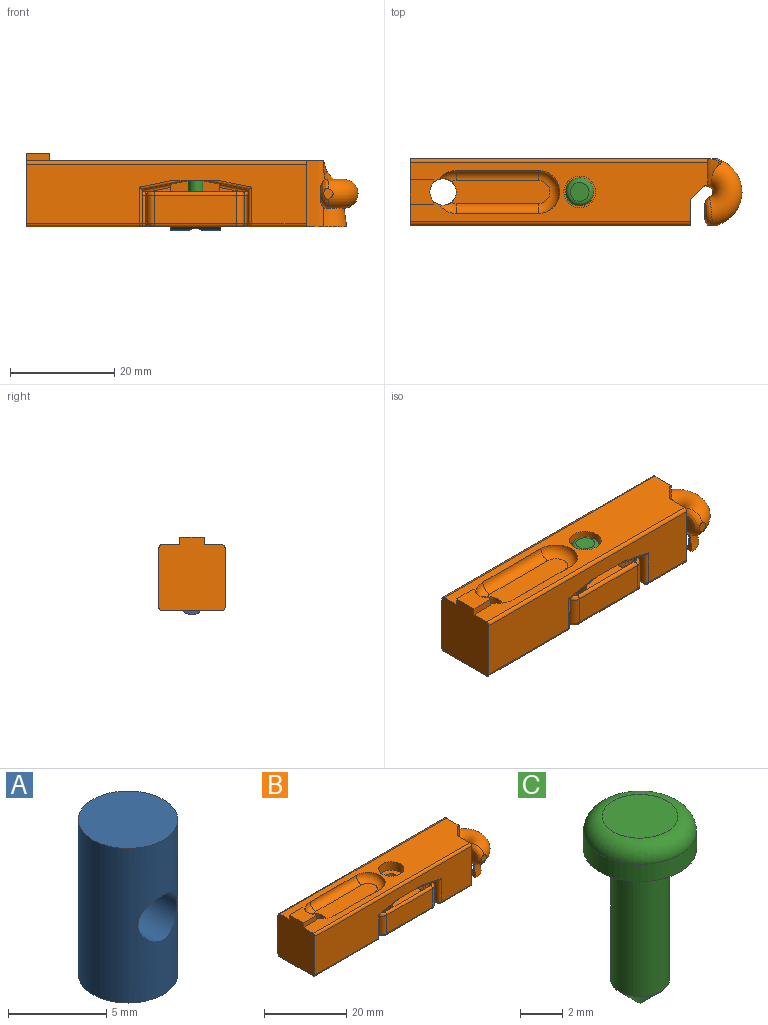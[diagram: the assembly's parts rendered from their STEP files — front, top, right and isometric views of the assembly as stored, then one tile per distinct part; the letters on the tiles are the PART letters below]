
ASSEMBLY  parts=3 mates=3
PART A: 4 faces, bbox 5.1x5.1x9.7 mm
  f0: cylinder r=2.54mm len=9.65mm, axis (0,0,-1), area 141.2mm2, adj f1,f2,f3
  f1: plane 5.08x5.08mm, normal (0,0,1), area 20.3mm2, adj f0
  f2: plane 5.08x5.08mm, normal (0,0,-1), area 20.3mm2, adj f0
  f3: cylinder r=1.4mm len=5.08mm, axis (0,-1,0), area 41mm2, adj f0
PART B: 172 faces, bbox 90.7x40.7x41.1 mm
  f0: plane 8.64x3.18mm, normal (0,0,-1), area 25.9mm2, adj f3,f124,f129,f130,f133,f134
  f1: torus R=3.81mm, axis (0,0,-1), area 204mm2, adj f6,f7,f10,f14,f29,f30,f33,f34
  f2: plane 57.24x11.49mm, normal (0,0,-1), area 414.8mm2, adj f8,f10,f15,f19,f26,f27,f45,f72
  f3: plane 9.4x1.14mm, normal (0,1,0), area 10.6mm2, adj f0,f60,f61,f68,f124,f129
  f4: plane 8.49x6.71mm, normal (-1,0,0), area 41.2mm2, adj f40,f45,f67,f140,f147,f148,f149,f153
  f5: cylinder r=1.59mm len=3.18mm, axis (0,0,1), area 12.8mm2, adj f38,f40,f41,f42,f43
  f6: cylinder r=6.35mm len=4.55mm, axis (0,0,-1), area 6.7mm2, adj f1,f14,f30,f35,f107,f157
  f7: plane 0.36x0.18mm, normal (0.91,-0.42,0), area 0mm2, adj f1,f29,f36
  f8: plane 2.9x1.42mm, normal (1,0,0), area 1.8mm2, adj f2,f10,f107
  f9: plane 57.24x11.49mm, normal (0,0,1), area 398mm2, adj f10,f11,f12,f15,f17,f18,f19,f21
  f10: cylinder r=1.27mm len=12.7mm, axis (0,0,-1), area 13.5mm2, adj f1,f2,f8,f9,f26,f28,f37,f107
  f11: plane 1.4x0.55mm, normal (1,0,0), area 0.8mm2, adj f9,f16,f18,f19
  f12: plane 1.4x0.55mm, normal (1,0,0), area 0.8mm2, adj f9,f16,f17,f19
  f13: plane 53.83x11.43mm, normal (0,-1,0), area 445mm2, adj f15,f27,f41,f109,f110,f111,f137,f140
  f14: plane 85.34x37.81mm, normal (0,1,0), area 656.6mm2, adj f1,f6,f15,f29,f154,f156
  f15: plane 14.1x12.7mm, normal (-1,0,0), area 167.5mm2, adj f2,f9,f13,f14,f16,f17,f18,f110
  f16: plane 4.72x4.57mm, normal (0,0,1), area 19.7mm2, adj f11,f12,f15,f17,f18,f19
  f17: plane 4.57x1.4mm, normal (0,-1,0), area 6.4mm2, adj f9,f12,f15,f16
  f18: plane 4.57x1.4mm, normal (0,1,0), area 6.4mm2, adj f9,f11,f15,f16
  f19: cylinder r=2.54mm len=14.1mm, axis (0,0,-1), area 194.8mm2, adj f2,f9,f11,f12,f16,f20,f21,f25
  f20: plane 18.94x4.45mm, normal (0,0,1), area 79.2mm2, adj f19,f21,f22,f23,f24,f25
  f21: torus R=2.22mm, axis (0,0,1), area 7.4mm2, adj f9,f19,f20,f22
  f22: cylinder r=1.91mm len=15.75mm, axis (1,0,0), area 47.1mm2, adj f9,f20,f21,f23
  f23: torus R=2.22mm, axis (0,0,1), area 32.3mm2, adj f9,f20,f22,f24
  f24: cylinder r=1.91mm len=15.75mm, axis (-1,0,0), area 47.1mm2, adj f9,f20,f23,f25
  f25: torus R=2.22mm, axis (0,0,1), area 7.4mm2, adj f9,f19,f20,f24
  f26: plane 12.7x2.42mm, normal (0.71,-0.71,0), area 43.5mm2, adj f2,f9,f10,f27
  f27: plane 12.7x4.83mm, normal (1,0,0), area 61.1mm2, adj f2,f9,f13,f26,f141,f160
  f28: plane 2.9x1.42mm, normal (1,0,0), area 1.8mm2, adj f9,f10,f108
  f29: cylinder r=6.35mm len=4.55mm, axis (0,0,-1), area 6.7mm2, adj f1,f7,f14,f36,f108,f155
  f30: plane 0.36x0.18mm, normal (0.91,-0.42,0), area 0mm2, adj f1,f6,f35
  f31: plane 3.12x3.05mm, normal (-1,0,0), area 7.5mm2, adj f34
  f32: plane 1.65x0.71mm, normal (-0.71,0.71,0), area 1.3mm2, adj f34
  f33: plane 28.49x28.17mm, normal (0,-1,0), area 2.8mm2, adj f1,f34
  f34: bspline ~5.59x5.58mm, area 25.5mm2, adj f1,f31,f32,f33,f101
  f35: cylinder r=1.27mm len=1.27mm, axis (0.42,0.91,0), area 0.8mm2, adj f1,f6,f30,f107
  f36: cylinder r=1.27mm len=1.27mm, axis (-0.42,-0.91,0), area 0.8mm2, adj f1,f7,f29,f108
  f37: bspline ~2.74x1.21mm, area 0mm2, adj f1,f10
  f38: plane 6.1x6.1mm, normal (0,0,1), area 21.3mm2, adj f5,f39
  f39: cylinder r=3.05mm len=6.1mm, axis (0,0,1), area 48.6mm2, adj f9,f38
  f40: plane 8.93x7.66mm, normal (-0.2,0,-0.98), area 68.5mm2, adj f4,f5,f41,f42,f137,f158
  f41: plane 9.02x5.49mm, normal (0,0,-1), area 13.5mm2, adj f5,f13,f40,f43,f109,f137
  f42: plane 2.54x1.04mm, normal (0,0,-1), area 1.3mm2, adj f5,f40,f43,f69
  f43: plane 8.99x7.72mm, normal (0.2,0,-0.98), area 68.8mm2, adj f5,f41,f42,f44,f109,f159
  f44: plane 8.49x6.71mm, normal (1,0,0), area 41.2mm2, adj f43,f45,f67,f111,f112,f113,f116,f117
  f45: plane 21.59x7.56mm, normal (0,-1,0), area 93.5mm2, adj f2,f4,f44,f69,f70,f71,f113,f153
  f46: plane 5.46x2.54mm, normal (0,-1,0), area 13.9mm2, adj f47,f117,f121,f162
  f47: cylinder r=0.76mm len=5.46mm, axis (0,0,-1), area 13.1mm2, adj f46,f48,f123,f163
  f48: plane 5.46x0.89mm, normal (0,1,0), area 4.9mm2, adj f47,f49,f127,f164
  f49: cylinder r=1.52mm len=5.46mm, axis (0,0,-1), area 26.1mm2, adj f48,f50,f132,f165
  f50: plane 15.75x5.46mm, normal (0,-1,0), area 86mm2, adj f49,f51,f134,f166
  f51: cylinder r=1.52mm len=5.46mm, axis (0,0,-1), area 26.1mm2, adj f50,f52,f136,f167
  f52: plane 5.46x0.89mm, normal (0,1,0), area 4.9mm2, adj f51,f53,f139,f168
  f53: cylinder r=0.76mm len=5.46mm, axis (0,0,-1), area 13.1mm2, adj f52,f54,f143,f169
  f54: plane 5.46x2.54mm, normal (0,-1,0), area 13.9mm2, adj f53,f146,f147,f170
  f55: plane 6.1x2.54mm, normal (0,1,0), area 15.5mm2, adj f56,f67,f149,f150
  f56: cylinder r=1.52mm len=6.1mm, axis (0,0,-1), area 29.2mm2, adj f55,f57,f67,f145
  f57: plane 6.1x0.89mm, normal (0,-1,0), area 5.4mm2, adj f56,f58,f67,f142
  f58: cylinder r=0.76mm len=6.1mm, axis (0,0,-1), area 14.6mm2, adj f57,f59,f67,f138
  f59: plane 6.1x2.54mm, normal (0,1,0), area 15.5mm2, adj f58,f67,f128,f135
  f60: plane 6.1x3.05mm, normal (1,0,0), area 16.5mm2, adj f3,f67,f68,f128,f129
  f61: plane 6.1x3.05mm, normal (-1,0,0), area 16.5mm2, adj f3,f67,f68,f124,f125
  f62: plane 6.1x2.54mm, normal (0,1,0), area 15.5mm2, adj f63,f67,f125,f131
  f63: cylinder r=0.76mm len=6.1mm, axis (0,0,-1), area 14.6mm2, adj f62,f64,f67,f126
  f64: plane 6.1x0.89mm, normal (0,-1,0), area 5.4mm2, adj f63,f65,f67,f122
  f65: cylinder r=1.52mm len=6.1mm, axis (0,0,-1), area 29.2mm2, adj f64,f66,f67,f120
  f66: plane 6.1x2.54mm, normal (0,1,0), area 15.5mm2, adj f65,f67,f112,f118
  f67: plane 20.32x5.33mm, normal (0,0,1), area 39.9mm2, adj f4,f44,f55,f56,f57,f58,f59,f60
  f68: plane 9.4x5.59mm, normal (0,0.99,-0.11), area 52.9mm2, adj f3,f60,f61,f67
  f69: plane 9.41x7.12mm, normal (0,-1,-0.09), area 64.7mm2, adj f42,f45,f70,f71,f158,f159
  f70: plane 6.47x0.62mm, normal (1,0,0), area 1.8mm2, adj f45,f69,f158
  f71: plane 6.47x0.62mm, normal (-1,0,0), area 1.8mm2, adj f45,f69,f159
  f72: plane 1.27x0.88mm, normal (0,-1,0), area 1.1mm2, adj f2,f73,f82,f83
  f73: plane 1.27x0.39mm, normal (-1,0,0), area 0.5mm2, adj f2,f72,f74,f83
  f74: plane 1.48x1.27mm, normal (0,-1,0), area 1.9mm2, adj f2,f73,f75,f83
  f75: plane 1.27x0.39mm, normal (1,0,0), area 0.5mm2, adj f2,f74,f76,f83
  f76: plane 5.09x1.27mm, normal (0.98,0.19,0), area 6.6mm2, adj f2,f75,f77,f83
  f77: plane 1.27x1.1mm, normal (0,-1,0), area 1.4mm2, adj f2,f76,f78,f83
  f78: plane 5.09x1.27mm, normal (-0.98,-0.18,0), area 6.6mm2, adj f2,f77,f79,f83
  f79: plane 1.32x1.27mm, normal (-1,0,0), area 1.7mm2, adj f2,f78,f80,f83
  f80: plane 2.53x1.27mm, normal (0,1,0), area 3.2mm2, adj f2,f79,f81,f83
  f81: plane 1.27x0.88mm, normal (0.61,0.79,0), area 1.4mm2, adj f2,f80,f82,f83
  f82: plane 1.27x0.64mm, normal (1,0,0), area 0.8mm2, adj f2,f72,f81,f83
  f83: plane 6.41x3.41mm, normal (0,0,-1), area 9.1mm2, adj f72,f73,f74,f75,f76,f77,f78,f79
  f84: plane 1.27x1.26mm, normal (0,1,0), area 1.6mm2, adj f2,f85,f94,f95
  f85: plane 1.27x0.88mm, normal (0.61,0.79,0), area 1.4mm2, adj f2,f84,f86,f95
  f86: plane 1.27x0.64mm, normal (1,0,0), area 0.8mm2, adj f2,f85,f87,f95
  f87: plane 1.27x0.88mm, normal (0,-1,0), area 1.1mm2, adj f2,f86,f88,f95
  f88: plane 3.81x1.27mm, normal (1,0,0), area 4.8mm2, adj f2,f87,f89,f95
  f89: plane 1.28x1.27mm, normal (0,1,0), area 1.6mm2, adj f2,f88,f90,f95
  f90: plane 1.28x1.27mm, normal (1,0,0), area 1.6mm2, adj f2,f89,f91,f95
  f91: plane 3.81x1.27mm, normal (0,-1,0), area 4.8mm2, adj f2,f90,f92,f95
  f92: plane 1.28x1.27mm, normal (-1,0,0), area 1.6mm2, adj f2,f91,f93,f95
  f93: plane 1.28x1.27mm, normal (0,1,0), area 1.6mm2, adj f2,f92,f94,f95
  f94: plane 5.13x1.27mm, normal (-1,0,0), area 6.5mm2, adj f2,f84,f93,f95
  f95: plane 6.41x3.81mm, normal (0,0,-1), area 12.2mm2, adj f84,f85,f86,f87,f88,f89,f90,f91
  f96: plane 3.56x1.16mm, normal (-0.94,0.34,0), area 2.6mm2, adj f1,f97,f98,f99
  f97: cone r=3.94mm half-angle=8deg, axis (0,0,-1), area 17mm2, adj f1,f96,f98,f100
  f98: plane 3.88x3.32mm, normal (0,0,-1), area 5.4mm2, adj f96,f97,f99,f100
  f99: cone r=3.68mm half-angle=8deg, axis (0,0,1), area 14mm2, adj f1,f96,f98,f100
  f100: plane 3.56x1.23mm, normal (0.09,-1,0), area 2.6mm2, adj f1,f97,f98,f99
  f101: torus R=3.81mm, axis (0,0,-1), area 0.2mm2, adj f34,f102,f103,f104
  f102: plane 3.56x1.24mm, normal (-1,0,0), area 2.6mm2, adj f101,f103,f104,f106
  f103: cone r=3.94mm half-angle=8deg, axis (0,0,-1), area 22.3mm2, adj f1,f101,f102,f105,f106
  f104: cone r=3.68mm half-angle=8deg, axis (0,0,1), area 18.3mm2, adj f1,f101,f102,f105,f106
  f105: plane 3.56x1.23mm, normal (0.09,1,0), area 2.6mm2, adj f1,f103,f104,f106
  f106: plane 4.41x4.15mm, normal (0,0,-1), area 7mm2, adj f102,f103,f104,f105
  f107: bspline ~8.28x7.39mm, area 18.9mm2, adj f1,f2,f6,f8,f10,f35,f157
  f108: bspline ~8.28x7.4mm, area 19mm2, adj f1,f9,f10,f28,f29,f36,f155
  f109: cylinder r=0.64mm len=9.53mm, axis (-0.98,0,-0.2), area 8.2mm2, adj f13,f41,f43,f111
  f110: cylinder r=0.64mm len=21.72mm, axis (1,0,0), area 21.7mm2, adj f2,f13,f15,f114
  f111: cylinder r=0.64mm len=7mm, axis (0,0,-1), area 6.7mm2, adj f13,f44,f109,f114
  f112: cylinder r=0.64mm len=6.1mm, axis (0,0,1), area 6.1mm2, adj f44,f66,f67,f115
  f113: cylinder r=0.64mm len=2.92mm, axis (0,1,0), area 2.9mm2, adj f2,f44,f45,f115
  f114: sphere r=0.64mm, area 0.6mm2, adj f110,f111,f116
  f115: torus R=1.27mm, axis (0,0,1), area 1.3mm2, adj f2,f112,f113,f118,f119
  f116: cylinder r=0.64mm len=3.3mm, axis (0,1,0), area 3.3mm2, adj f2,f44,f114,f119
  f117: cylinder r=0.64mm len=5.46mm, axis (0,0,1), area 5.4mm2, adj f44,f46,f119,f161
  f118: cylinder r=0.64mm len=2.54mm, axis (-1,0,0), area 1.9mm2, adj f66,f115,f120,f121
  f119: torus R=1.27mm, axis (0,0,1), area 1.3mm2, adj f2,f115,f116,f117,f121
  f120: torus R=0.89mm, axis (0,0,1), area 3.2mm2, adj f65,f118,f122,f123
  f121: cylinder r=0.64mm len=2.54mm, axis (1,0,0), area 1.9mm2, adj f46,f118,f119,f123
  f122: cylinder r=0.64mm len=0.89mm, axis (1,0,0), area 0.7mm2, adj f64,f120,f126,f127
  f123: torus R=1.4mm, axis (0,0,1), area 2.1mm2, adj f47,f120,f121,f127
  f124: cylinder r=0.64mm len=2.41mm, axis (0,-1,0), area 2.4mm2, adj f0,f3,f61,f130
  f125: cylinder r=0.64mm len=6.1mm, axis (0,0,1), area 6.1mm2, adj f61,f62,f67,f130
  f126: torus R=1.4mm, axis (0,0,1), area 2.1mm2, adj f63,f122,f131,f132
  f127: cylinder r=0.64mm len=0.89mm, axis (-1,0,0), area 0.7mm2, adj f48,f122,f123,f132
  f128: cylinder r=0.64mm len=6.1mm, axis (0,0,1), area 6.1mm2, adj f59,f60,f67,f133
  f129: cylinder r=0.64mm len=2.41mm, axis (0,1,0), area 2.4mm2, adj f0,f3,f60,f133
  f130: torus R=1.27mm, axis (0,0,1), area 1.2mm2, adj f0,f124,f125,f131,f134
  f131: cylinder r=0.64mm len=2.54mm, axis (-1,0,0), area 1.9mm2, adj f62,f126,f130,f134
  f132: torus R=0.89mm, axis (0,0,1), area 3.2mm2, adj f49,f126,f127,f134
  f133: torus R=1.27mm, axis (0,0,1), area 1.2mm2, adj f0,f128,f129,f134,f135
  f134: cylinder r=0.64mm len=15.75mm, axis (1,0,0), area 14.1mm2, adj f0,f50,f130,f131,f132,f133,f135,f136
  f135: cylinder r=0.64mm len=2.54mm, axis (-1,0,0), area 1.9mm2, adj f59,f133,f134,f138
  f136: torus R=0.89mm, axis (0,0,1), area 3.2mm2, adj f51,f134,f138,f139
  f137: cylinder r=0.64mm len=9.53mm, axis (-0.98,0,0.2), area 8.2mm2, adj f13,f40,f41,f140
  f138: torus R=1.4mm, axis (0,0,1), area 2.1mm2, adj f58,f135,f136,f142
  f139: cylinder r=0.64mm len=0.89mm, axis (-1,0,0), area 0.7mm2, adj f52,f136,f142,f143
  f140: cylinder r=0.64mm len=7mm, axis (0,0,1), area 6.7mm2, adj f4,f13,f137,f144
  f141: cylinder r=0.64mm len=10.52mm, axis (1,0,0), area 10.5mm2, adj f2,f13,f27,f144
  f142: cylinder r=0.64mm len=0.89mm, axis (1,0,0), area 0.7mm2, adj f57,f138,f139,f145
  f143: torus R=1.4mm, axis (0,0,1), area 2.1mm2, adj f53,f139,f145,f146
  f144: sphere r=0.64mm, area 0.6mm2, adj f140,f141,f148
  f145: torus R=0.89mm, axis (0,0,1), area 3.2mm2, adj f56,f142,f143,f150
  f146: cylinder r=0.64mm len=2.54mm, axis (1,0,0), area 1.9mm2, adj f54,f143,f150,f151
  f147: cylinder r=0.64mm len=5.46mm, axis (0,0,1), area 5.4mm2, adj f4,f54,f151,f171
  f148: cylinder r=0.64mm len=3.3mm, axis (0,-1,0), area 3.3mm2, adj f2,f4,f144,f151
  f149: cylinder r=0.64mm len=6.1mm, axis (0,0,1), area 6.1mm2, adj f4,f55,f67,f152
  f150: cylinder r=0.64mm len=2.54mm, axis (-1,0,0), area 1.9mm2, adj f55,f145,f146,f152
  f151: torus R=1.27mm, axis (0,0,1), area 1.3mm2, adj f2,f146,f147,f148,f152
  f152: torus R=1.27mm, axis (0,0,1), area 1.3mm2, adj f2,f149,f150,f151,f153
  f153: cylinder r=0.64mm len=2.92mm, axis (0,-1,0), area 2.9mm2, adj f2,f4,f45,f152
  f154: cylinder r=0.64mm len=57.15mm, axis (1,0,0), area 57mm2, adj f9,f14,f15,f155
  f155: torus R=5.71mm, axis (0,0,1), area 0.1mm2, adj f9,f29,f108,f154
  f156: cylinder r=0.64mm len=57.15mm, axis (-1,0,0), area 57mm2, adj f2,f14,f15,f157
  f157: torus R=5.71mm, axis (0,0,1), area 0.1mm2, adj f2,f6,f107,f156
  f158: cylinder r=0.64mm len=9.14mm, axis (-0.98,0,0.2), area 5.7mm2, adj f4,f40,f45,f69,f70
  f159: cylinder r=0.64mm len=9.14mm, axis (-0.98,0,-0.2), area 5.7mm2, adj f43,f44,f45,f69,f71
  f160: cylinder r=0.64mm len=53.83mm, axis (-1,0,0), area 53.7mm2, adj f9,f13,f15,f27
  f161: torus R=1.27mm, axis (0,0,1), area 0.8mm2, adj f44,f67,f117,f162
  f162: cylinder r=0.64mm len=2.54mm, axis (-1,0,0), area 2.5mm2, adj f46,f67,f161,f163
  f163: torus R=1.4mm, axis (0,0,1), area 3.1mm2, adj f47,f67,f162,f164
  f164: cylinder r=0.64mm len=0.89mm, axis (1,0,0), area 0.9mm2, adj f48,f67,f163,f165
  f165: torus R=0.89mm, axis (0,0,1), area 4.1mm2, adj f49,f67,f164,f166
  f166: cylinder r=0.64mm len=15.75mm, axis (-1,0,0), area 15.7mm2, adj f50,f67,f165,f167
  f167: torus R=0.89mm, axis (0,0,1), area 4.1mm2, adj f51,f67,f166,f168
  f168: cylinder r=0.64mm len=0.89mm, axis (1,0,0), area 0.9mm2, adj f52,f67,f167,f169
  f169: torus R=1.4mm, axis (0,0,1), area 3.1mm2, adj f53,f67,f168,f170
  f170: cylinder r=0.64mm len=2.54mm, axis (-1,0,0), area 2.5mm2, adj f54,f67,f169,f171
  f171: torus R=1.27mm, axis (0,0,1), area 0.8mm2, adj f4,f67,f147,f170
PART C: 7 faces, bbox 5.8x5.8x10.8 mm
  f0: cylinder r=2.69mm len=5.38mm, axis (0,0,-1), area 17.2mm2, adj f2,f3
  f1: plane 3.61x3.61mm, normal (0,0,1), area 10.2mm2, adj f3
  f2: plane 5.38x5.38mm, normal (0,0,-1), area 16.6mm2, adj f0,f4
  f3: torus R=1.8mm, axis (0,0,1), area 20.8mm2, adj f0,f1
  f4: cylinder r=1.4mm len=7.62mm, axis (0,0,1), area 66.9mm2, adj f2,f6
  f5: plane 0.25x0.25mm, normal (0,0,-1), area 0.1mm2, adj f6
  f6: cone r=1.4mm half-angle=45deg, axis (0,0,1), area 8.6mm2, adj f4,f5
PLACE A rot(axis=(0.58,0.58,0.58),120deg) t=(-10.8,-5.39,-20.94)mm
PLACE B t=(-38.55,-11.74,-22.76)mm
PLACE C t=(-5.97,-5.39,-12.6)mm
MATE cylindrical A.f3 <-> C.f4  axis (0,0,-1) through (-5.97,-5.39,-23.51)mm
MATE planar C.f0 <-> B.f5  axis (0,0,-1) through (-5.97,-5.39,-12.6)mm
MATE cylindrical B.f5 <-> C.f0  axis (0,0,1) through (-5.97,-5.39,-12.6)mm
